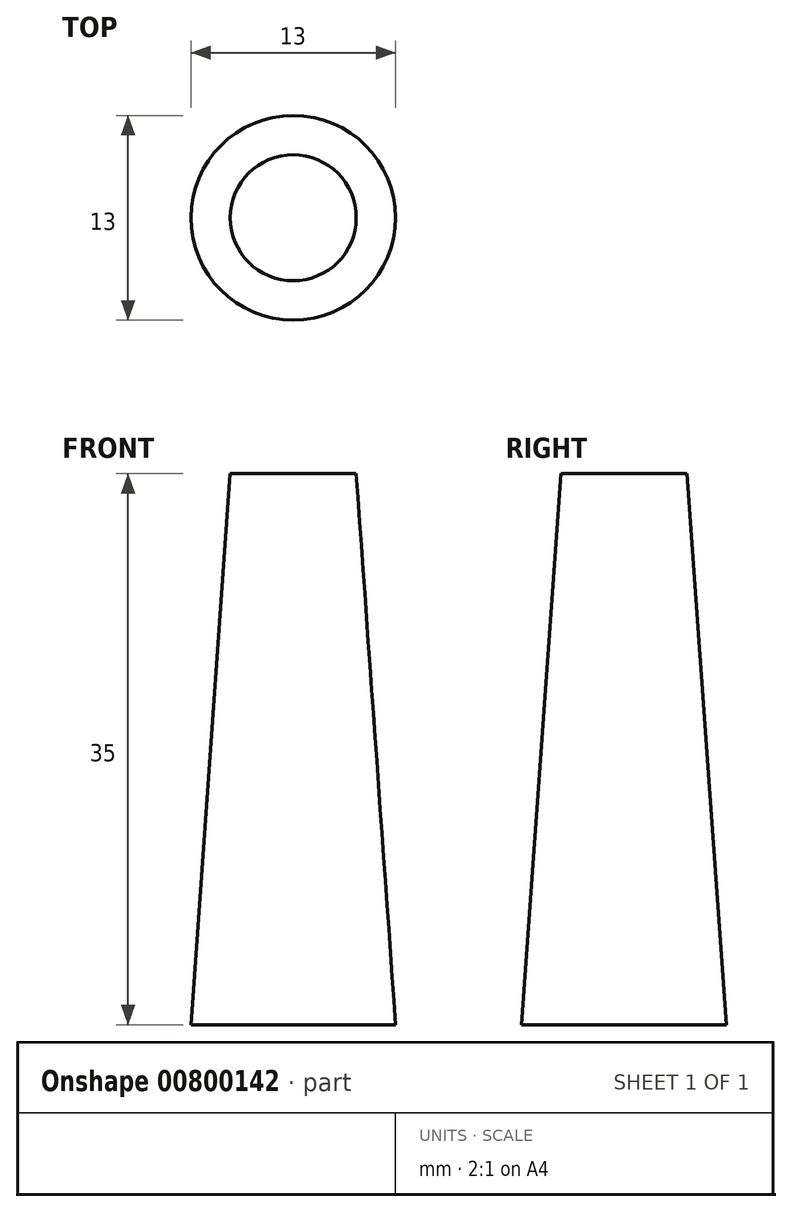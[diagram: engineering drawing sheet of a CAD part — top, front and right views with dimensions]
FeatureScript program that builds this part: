
annotation { "Feature Type Name" : "Feature", "Feature Type Description" : "" }
export const myFeature = defineFeature(function(context is Context, id is Id, definition is map)
    precondition{}
    {
        {
            var Q0;
            Q0=qCreatedBy(makeId("Front.planeOp"),FACE);
            var sketch = newSketch(context, id + "F0", { "sketchPlane" : qUnion([Q0])});
            skLineSegment(sketch, "E0", {"start": v(0, 0) * mm, "end": v(-6.5, 0) * mm});
            skLineSegment(sketch, "E1", {"start": v(-6.5, 0) * mm, "end": v(-4, 35) * mm});
            skLineSegment(sketch, "E2", {"start": v(-4, 35) * mm, "end": v(0, 35) * mm});
            skLineSegment(sketch, "E3", {"start": v(0, 35) * mm, "end": v(0, 0) * mm});
            skSolve(sketch);
        }
        {
            var Q0;
            Q0=makeQuery(id+"F0.imprint","IMPRINT",FACE,{"disambiguationData":[TD([[makeQuery(id+"F0.imprint","IMPRINT",EDGE,{"derivedFrom":sQuery(id+"F0.wireOp",EDGE,"E0")}),-1.0]])]});
            var Q1;
            Q1=sQuery(id+"F0.wireOp",EDGE,"E3");
            revolve(context, id + "F1", {"surfaceOperationType" : NewSurfaceOperationType.NEW, "entities" : qUnion([Q0]), "axis" : qUnion([Q1]), "revolveType" : RevolveType.FULL});
        }
    });
